# Revit family: Bticino_Hotel_UX_TOUCH_Command_Touch_panel_scenario
name_source: partatom
category: Equipement électrique
units: mm (PartAtom-declared; Revit-internal decimal feet)

## family parameters
Configuration du panneau = Deux colonnes, circuits au sein
Cote de connecteur circulaire = Utiliser le diamètre
Couper avec des vides une fois chargée = Non
Hôte = Face
Partagée = Non
Point de calcul de pièce = Non
Type d'élément = Tableau de raccordement

## types (6) — shared parameters
Built-in depth = 30 mm  [stored 0.0984252 ft]
Degree of impact strength (IK) = IK02
Degree of protection (IP) = IP20
Elévation par défaut = 1300 mm  [stored 4.26509 ft]
Fabricant = Legrand
General Conditions of Use = https://export.legrand.com
Mounting method = Flush mounted (plaster)
Operating / setting temperature MIN-MAX (°C) = 0-40
Other bus systems = Other
Overall depth = 42 mm  [stored 0.137795 ft]
Overall height = 93 mm  [stored 0.305118 ft]
Overall width = 129 mm  [stored 0.423228 ft]
Programmable = Oui
Programming way = Computer
Standby consuption (mA) = 8
Storage temperature MIN-MAX (°C) = -20-70
Supply frequency MIN-MAX ( Hz) = 0-0
Type of surface = Brilliant
URL = http://www.legrandoc.com
Web configurator = https://uxforupscalehotel.legrand.com
With LED indication = Oui

## per-type parameters (varying)
| type | Colour | Command | Description | Material | Modèle | Number of buttons | With room temperature controller |
| Thermostat_Bedside Pannel Black | black | Tête de lit | Bedside panel SCS | LEGRAND - Black plastic | FL4653 | 10 | Oui |
| 4 scenario Black | black | 4 touches | 4G touch plate | LEGRAND - Black plastic | FL4655 | 4 | Non |
| 6 scenario Black | black | 6 touches | 6G touch plate | LEGRAND - Black plastic | FL4652 | 6 | Non |
| 6 scenario White | White | 6 touches | 6G touch plate | LEGRAND - White plastic | FL4652W | 6 | Non |
| Thermostat_Bedside Pannel White | White | Tête de lit | Bedside panel SCS | LEGRAND - White plastic | FL4653W | 10 | Oui |
| 4 scenario White | White | 4 touches | 4G touch plate | LEGRAND - White plastic | FL4655W | 4 | Non |

note: [stored X ft] marks values corroborated as IEEE doubles in the binary element streams (Revit-internal decimal feet)
